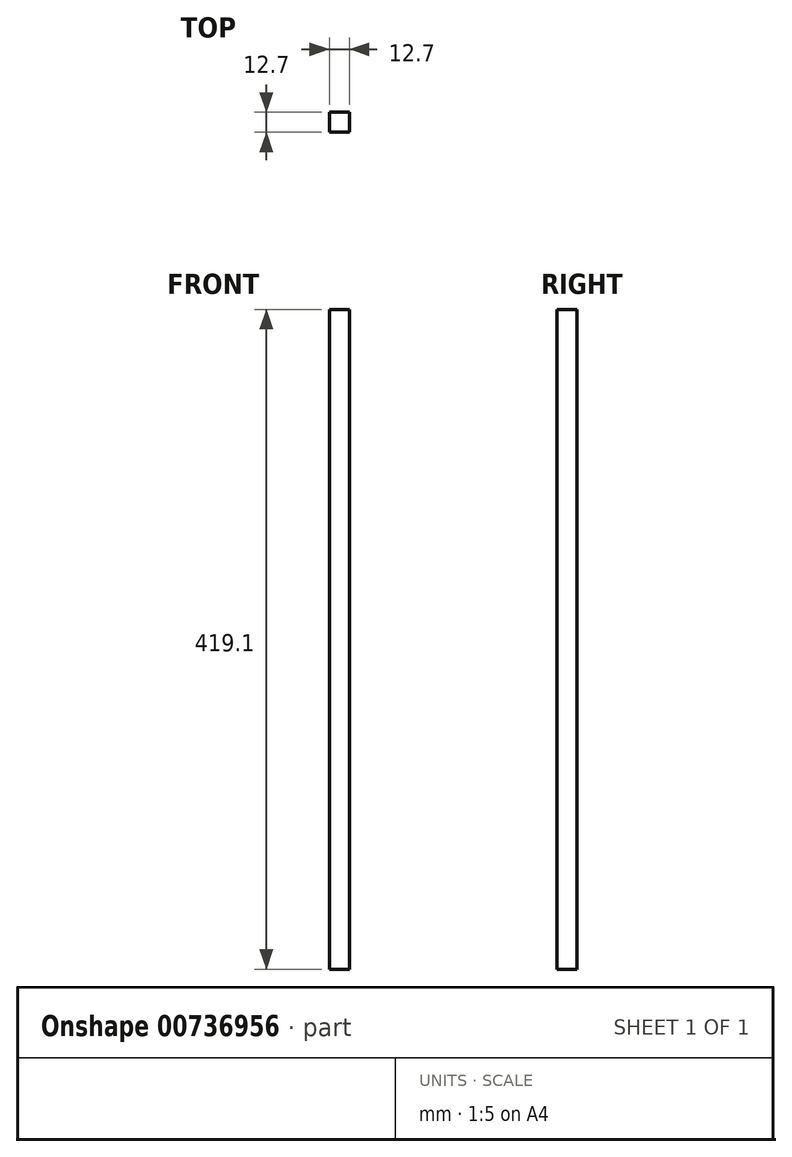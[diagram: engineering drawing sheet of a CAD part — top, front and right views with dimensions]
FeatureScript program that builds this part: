
annotation { "Feature Type Name" : "Feature", "Feature Type Description" : "" }
export const myFeature = defineFeature(function(context is Context, id is Id, definition is map)
    precondition{}
    {
        {
            var Q0;
            Q0=qCreatedBy(makeId("Front.planeOp"),FACE);
            var sketch = newSketch(context, id + "F0", { "sketchPlane" : qUnion([Q0])});
            skLineSegment(sketch, "E0.bottom", {"start": v(6.35, -209.55) * mm, "end": v(-6.35, -209.55) * mm});
            skLineSegment(sketch, "E0.top", {"start": v(6.35, 209.55) * mm, "end": v(-6.35, 209.55) * mm});
            skLineSegment(sketch, "E0.left", {"start": v(6.35, -209.55) * mm, "end": v(6.35, 209.55) * mm});
            skLineSegment(sketch, "E0.right", {"start": v(-6.35, -209.55) * mm, "end": v(-6.35, 209.55) * mm});
            skPoint(sketch, "E0.middle", {"position": v(0, 0) * mm});
            skSolve(sketch);
        }
        {
            var Q0;
            Q0 = qSketchRegion(id + "F0", true);
            extrude(context, id + "F1", {"entities" : qUnion([Q0]), "depth" : 12.7 * mm, "offsetDistance" : 25.4 * mm});
        }
    });
